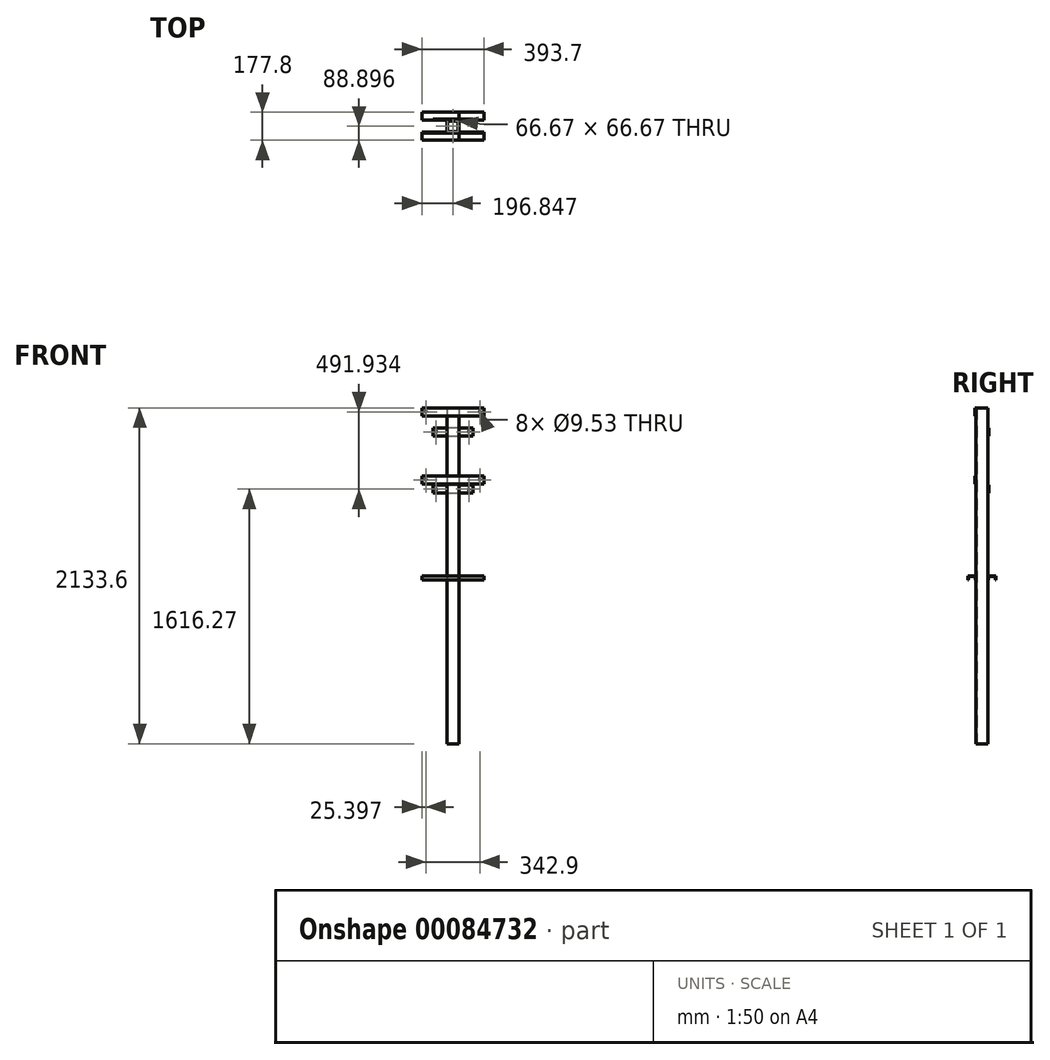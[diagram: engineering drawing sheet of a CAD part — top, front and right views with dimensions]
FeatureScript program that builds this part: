
annotation { "Feature Type Name" : "Feature", "Feature Type Description" : "" }
export const myFeature = defineFeature(function(context is Context, id is Id, definition is map)
    precondition{}
    {
        {
            var Q0;
            Q0=qCreatedBy(makeId("Top.planeOp"),FACE);
            var sketch = newSketch(context, id + "F0", { "sketchPlane" : qUnion([Q0])});
            skLineSegment(sketch, "E0.bottom", {"start": v(-38.12, 37.72) * mm, "end": v(38.08, 37.72) * mm});
            skLineSegment(sketch, "E0.top", {"start": v(-38.12, -38.48) * mm, "end": v(38.08, -38.48) * mm});
            skLineSegment(sketch, "E0.left", {"start": v(-38.12, 37.72) * mm, "end": v(-38.12, -38.48) * mm});
            skLineSegment(sketch, "E0.right", {"start": v(38.08, 37.72) * mm, "end": v(38.08, -38.48) * mm});
            skLineSegment(sketch, "E1.0", {"start": v(-33.36, 32.95) * mm, "end": v(-33.36, -33.72) * mm});
            skLineSegment(sketch, "E1.1", {"start": v(-33.36, 32.95) * mm, "end": v(33.31, 32.95) * mm});
            skLineSegment(sketch, "E1.2", {"start": v(33.31, 32.95) * mm, "end": v(33.31, -33.72) * mm});
            skLineSegment(sketch, "E1.3", {"start": v(-33.36, -33.72) * mm, "end": v(33.31, -33.72) * mm});
            skSolve(sketch);
        }
        {
            var Q0;
            Q0=makeQuery(id+"F0.imprint","IMPRINT",FACE,{"disambiguationData":[TD([[makeQuery(id+"F0.imprint","IMPRINT",EDGE,{"derivedFrom":sQuery(id+"F0.wireOp",EDGE,"E0.bottom")}),-1.0]])]});
            extrude(context, id + "F1", {"entities" : qUnion([Q0]), "depth" : 2133.6 * mm});
        }
        {
            var Q0;
            Q0=makeQuery(id+"F1.opExtrude","CAP_FACE",FACE,{"disambiguationData":[OSD([sQuery(id+"F0.wireOp",EDGE,"E0.bottom"),sQuery(id+"F0.wireOp",EDGE,"E0.top"),sQuery(id+"F0.wireOp",EDGE,"E0.left"),sQuery(id+"F0.wireOp",EDGE,"E0.right"),sQuery(id+"F0.wireOp",EDGE,"E1.0"),sQuery(id+"F0.wireOp",EDGE,"E1.1"),sQuery(id+"F0.wireOp",EDGE,"E1.2"),sQuery(id+"F0.wireOp",EDGE,"E1.3")])],"isStart":false});
            var sketch = newSketch(context, id + "F2", { "sketchPlane" : qUnion([Q0])});
            skSolve(sketch);
        }
        {
            var Q0;
            Q0=makeQuery(id+"F2.imprint","IMPRINT",FACE,{"disambiguationData":[TD([[makeQuery(id+"F2.imprint","IMPRINT",EDGE,{"derivedFrom":makeQuery(id+"F1.opExtrude","CAP_EDGE",EDGE,{"disambiguationData":[OSD([sQuery(id+"F0.wireOp",EDGE,"E1.0")])],"isStart":false})}),1.0]])]});
            var sketch = newSketch(context, id + "F3", { "sketchPlane" : qUnion([Q0])});
            skSolve(sketch);
        }
        {
            var Q0;
            Q0=qSketchRegion(id+"F3",true);
            var Q1;
            Q1=makeQuery(id+"F2.imprint","IMPRINT",FACE,{"disambiguationData":[TD([[makeQuery(id+"F2.imprint","IMPRINT",EDGE,{"derivedFrom":makeQuery(id+"F1.opExtrude","CAP_EDGE",EDGE,{"disambiguationData":[OSD([sQuery(id+"F0.wireOp",EDGE,"E1.0")])],"isStart":false})}),1.0]])]});
            extrude(context, id + "F4", {"entities" : qUnion([Q0, Q1]), "oppositeDirection" : true, "depth" : 4.76 * mm});
        }
        {
            var Q0;
            Q0=makeQuery(id+"F1.opExtrude","SWEPT_FACE",FACE,{"disambiguationData":[OSD([sQuery(id+"F0.wireOp",EDGE,"E0.top")])]});
            var sketch = newSketch(context, id + "F5", { "sketchPlane" : qUnion([Q0])});
            skLineSegment(sketch, "E2", {"start": v(-38.12, 2133.6) * mm, "end": v(-196.87, 2133.6) * mm});
            skLineSegment(sketch, "E3", {"start": v(-196.87, 2133.6) * mm, "end": v(-196.87, 2082.8) * mm});
            skLineSegment(sketch, "E4", {"start": v(-196.87, 2082.8) * mm, "end": v(196.83, 2082.8) * mm});
            skLineSegment(sketch, "E5", {"start": v(196.83, 2082.8) * mm, "end": v(196.83, 2133.6) * mm});
            skLineSegment(sketch, "E6", {"start": v(-38.12, 2133.6) * mm, "end": v(38.08, 2133.6) * mm});
            skLineSegment(sketch, "E7", {"start": v(38.08, 2133.6) * mm, "end": v(196.83, 2133.6) * mm});
            skCircle(sketch, "E8", {"center": v(-171.47, 2108.2) * mm, "radius": 4.76 * mm});
            skCircle(sketch, "E9", {"center": v(171.43, 2108.2) * mm, "radius": 4.76 * mm});
            skLineSegment(sketch, "E10", {"start": v(-196.87, 1701.8) * mm, "end": v(-38.12, 1701.8) * mm});
            skLineSegment(sketch, "E11", {"start": v(-38.12, 1701.8) * mm, "end": v(38.08, 1701.8) * mm});
            skLineSegment(sketch, "E12", {"start": v(38.08, 1701.8) * mm, "end": v(196.83, 1701.8) * mm});
            skLineSegment(sketch, "E13", {"start": v(196.83, 1701.8) * mm, "end": v(196.83, 1650.99) * mm});
            skLineSegment(sketch, "E14", {"start": v(196.83, 1650.99) * mm, "end": v(-196.87, 1650.99) * mm});
            skLineSegment(sketch, "E15", {"start": v(-196.87, 1650.99) * mm, "end": v(-196.87, 1701.8) * mm});
            skCircle(sketch, "E16", {"center": v(171.43, 1676.4) * mm, "radius": 4.76 * mm});
            skCircle(sketch, "E17", {"center": v(-171.47, 1676.4) * mm, "radius": 4.76 * mm});
            skSolve(sketch);
        }
        {
            var Q0;
            {var subQ1=sQuery(id+"F5.wireOp",EDGE,"E10");Q0=makeQuery(id+"F5.imprint","IMPRINT",FACE,{"disambiguationData":[TD([[makeQuery(id+"F5.imprint","IMPRINT",EDGE,{"derivedFrom":subQ1}),-1.0]])]});}
            var Q1;
            {var subQ4=sQuery(id+"F5.wireOp",EDGE,"E12");Q1=makeQuery(id+"F5.imprint","IMPRINT",FACE,{"disambiguationData":[TD([[makeQuery(id+"F5.imprint","IMPRINT",EDGE,{"derivedFrom":subQ4}),-1.0]])]});}
            var Q2;
            {var subQ0=sQuery(id+"F5.wireOp",EDGE,"E11");Q2=makeQuery(id+"F5.imprint","IMPRINT",FACE,{"disambiguationData":[TD([[makeQuery(id+"F5.imprint","IMPRINT",EDGE,{"derivedFrom":subQ0}),-1.0]])]});}
            var Q3;
            {var subQ4=sQuery(id+"F5.wireOp",EDGE,"E2");Q3=makeQuery(id+"F5.imprint","IMPRINT",FACE,{"disambiguationData":[TD([[makeQuery(id+"F5.imprint","IMPRINT",EDGE,{"derivedFrom":subQ4}),1.0]])]});}
            var Q4;
            {var subQ6=sQuery(id+"F5.wireOp",EDGE,"E6");Q4=makeQuery(id+"F5.imprint","IMPRINT",FACE,{"disambiguationData":[TD([[makeQuery(id+"F5.imprint","IMPRINT",EDGE,{"derivedFrom":subQ6}),-1.0]])]});}
            var Q5;
            {var subQ1=sQuery(id+"F5.wireOp",EDGE,"E5");Q5=makeQuery(id+"F5.imprint","IMPRINT",FACE,{"disambiguationData":[TD([[makeQuery(id+"F5.imprint","IMPRINT",EDGE,{"derivedFrom":subQ1}),1.0]])]});}
            extrude(context, id + "F6", {"entities" : qUnion([Q0, Q1, Q2, Q3, Q4, Q5]), "operationType" : NewBodyOperationType.ADD, "depth" : 6.35 * mm});
        }
        {
            var Q0;
            Q0=makeQuery(id+"F1.opExtrude","SWEPT_FACE",FACE,{"disambiguationData":[OSD([sQuery(id+"F0.wireOp",EDGE,"E0.bottom")])]});
            var sketch = newSketch(context, id + "F7", { "sketchPlane" : qUnion([Q0])});
            skLineSegment(sketch, "E18", {"start": v(-126.98, 2006.6) * mm, "end": v(127.02, 2006.6) * mm});
            skLineSegment(sketch, "E19", {"start": v(127.02, 2006.6) * mm, "end": v(127.02, 1955.8) * mm});
            skLineSegment(sketch, "E20", {"start": v(127.02, 1955.8) * mm, "end": v(-126.98, 1955.8) * mm});
            skLineSegment(sketch, "E21", {"start": v(-126.98, 1955.8) * mm, "end": v(-126.98, 2006.6) * mm});
            skLineSegment(sketch, "E22", {"start": v(127.02, 1641.67) * mm, "end": v(127.02, 1590.87) * mm});
            skLineSegment(sketch, "E23", {"start": v(127.02, 1590.87) * mm, "end": v(-126.98, 1590.87) * mm});
            skLineSegment(sketch, "E24", {"start": v(-126.98, 1590.87) * mm, "end": v(-126.98, 1641.67) * mm});
            skLineSegment(sketch, "E25", {"start": v(127.02, 1641.67) * mm, "end": v(-126.98, 1641.67) * mm});
            skCircle(sketch, "E26", {"center": v(-101.58, 1981.2) * mm, "radius": 4.76 * mm});
            skCircle(sketch, "E27", {"center": v(106.39, 1981.2) * mm, "radius": 4.76 * mm});
            skCircle(sketch, "E28", {"center": v(-100.93, 1616.27) * mm, "radius": 4.76 * mm});
            skCircle(sketch, "E29", {"center": v(107.03, 1616.27) * mm, "radius": 4.76 * mm});
            skSolve(sketch);
        }
        {
            var Q0;
            {var subQ0=sQuery(id+"F7.wireOp",EDGE,"E21");Q0=makeQuery(id+"F7.imprint","IMPRINT",FACE,{"disambiguationData":[TD([[makeQuery(id+"F7.imprint","IMPRINT",EDGE,{"derivedFrom":subQ0}),-1.0]])]});}
            var Q1;
            {var subQ0=sQuery(id+"F7.wireOp",EDGE,"E19");Q1=makeQuery(id+"F7.imprint","IMPRINT",FACE,{"disambiguationData":[TD([[makeQuery(id+"F7.imprint","IMPRINT",EDGE,{"derivedFrom":subQ0}),-1.0]])]});}
            var Q2;
            {var subQ1=sQuery(id+"F7.wireOp",EDGE,"E22");Q2=makeQuery(id+"F7.imprint","IMPRINT",FACE,{"disambiguationData":[TD([[makeQuery(id+"F7.imprint","IMPRINT",EDGE,{"derivedFrom":subQ1}),-1.0]])]});}
            var Q3;
            {var subQ0=sQuery(id+"F7.wireOp",EDGE,"E18");var subQ1=sQuery(id+"F0.wireOp",EDGE,"E0.bottom");var subQ2=makeQuery(id+"F1.opExtrude","SWEPT_EDGE",EDGE,{"disambiguationData":[OSD([subQ1,sQuery(id+"F0.wireOp",EDGE,"E0.right")])]});var subQ3=makeQuery(id+"F7.imprint","INTERSECT",VERTEX,{"derivedFrom":[subQ2,subQ0]});Q3=makeQuery(id+"F7.imprint","IMPRINT",FACE,{"disambiguationData":[TD([[makeQuery(id+"F7.imprint","IMPRINT",EDGE,{"disambiguationData":[TD([[subQ3,-1.0]])],"derivedFrom":subQ0}),-1.0]])]});}
            var Q4;
            {var subQ0=sQuery(id+"F7.wireOp",EDGE,"E23");var subQ1=sQuery(id+"F0.wireOp",EDGE,"E0.bottom");var subQ2=makeQuery(id+"F1.opExtrude","SWEPT_EDGE",EDGE,{"disambiguationData":[OSD([subQ1,sQuery(id+"F0.wireOp",EDGE,"E0.left")])]});var subQ3=makeQuery(id+"F7.imprint","INTERSECT",VERTEX,{"derivedFrom":[subQ2,subQ0]});Q4=makeQuery(id+"F7.imprint","IMPRINT",FACE,{"disambiguationData":[TD([[makeQuery(id+"F7.imprint","IMPRINT",EDGE,{"disambiguationData":[TD([[subQ3,-1.0]])],"derivedFrom":subQ0}),-1.0]])]});}
            var Q5;
            {var subQ0=sQuery(id+"F7.wireOp",EDGE,"E24");Q5=makeQuery(id+"F7.imprint","IMPRINT",FACE,{"disambiguationData":[TD([[makeQuery(id+"F7.imprint","IMPRINT",EDGE,{"derivedFrom":subQ0}),-1.0]])]});}
            extrude(context, id + "F8", {"entities" : qUnion([Q0, Q1, Q2, Q3, Q4, Q5]), "operationType" : NewBodyOperationType.ADD, "depth" : 6.35 * mm});
        }
        {
            var Q0;
            Q0=makeQuery(id+"F1.opExtrude","SWEPT_FACE",FACE,{"disambiguationData":[OSD([sQuery(id+"F0.wireOp",EDGE,"E0.right")])]});
            var sketch = newSketch(context, id + "F9", { "sketchPlane" : qUnion([Q0])});
            skLineSegment(sketch, "E30", {"start": v(-38.48, 1066.8) * mm, "end": v(-89.28, 1066.8) * mm});
            skLineSegment(sketch, "E31", {"start": v(-89.28, 1066.8) * mm, "end": v(-89.28, 1041.4) * mm});
            skLineSegment(sketch, "E32", {"start": v(-89.28, 1041.4) * mm, "end": v(-86.1, 1041.4) * mm});
            skLineSegment(sketch, "E33", {"start": v(-86.1, 1041.4) * mm, "end": v(-86.1, 1063.62) * mm});
            skLineSegment(sketch, "E34", {"start": v(-86.1, 1063.62) * mm, "end": v(-41.66, 1063.62) * mm});
            skLineSegment(sketch, "E35", {"start": v(-41.66, 1063.62) * mm, "end": v(-41.66, 1041.4) * mm});
            skLineSegment(sketch, "E36", {"start": v(-41.66, 1041.4) * mm, "end": v(-38.48, 1041.4) * mm});
            skLineSegment(sketch, "E37", {"start": v(37.72, 1066.8) * mm, "end": v(88.52, 1066.8) * mm});
            skLineSegment(sketch, "E38", {"start": v(88.52, 1066.8) * mm, "end": v(88.52, 1041.4) * mm});
            skLineSegment(sketch, "E39", {"start": v(88.52, 1041.4) * mm, "end": v(85.34, 1041.4) * mm});
            skLineSegment(sketch, "E40", {"start": v(85.34, 1041.4) * mm, "end": v(85.34, 1063.62) * mm});
            skLineSegment(sketch, "E41", {"start": v(85.34, 1063.62) * mm, "end": v(40.9, 1063.62) * mm});
            skLineSegment(sketch, "E42", {"start": v(40.9, 1063.62) * mm, "end": v(40.9, 1041.4) * mm});
            skLineSegment(sketch, "E43", {"start": v(40.9, 1041.4) * mm, "end": v(37.72, 1041.4) * mm});
            skSolve(sketch);
        }
        {
            var Q0;
            Q0 = qSketchRegion(id + "F9", true);
            var Q1;
            {var subQ0=sQuery(id+"F9.wireOp",EDGE,"E30");Q1=makeQuery(id+"F9.imprint","IMPRINT",FACE,{"disambiguationData":[TD([[makeQuery(id+"F9.imprint","IMPRINT",EDGE,{"derivedFrom":subQ0}),1.0]])]});}
            var Q2;
            {var subQ0=sQuery(id+"F9.wireOp",EDGE,"E37");Q2=makeQuery(id+"F9.imprint","IMPRINT",FACE,{"disambiguationData":[TD([[makeQuery(id+"F9.imprint","IMPRINT",EDGE,{"derivedFrom":subQ0}),-1.0]])]});}
            extrude(context, id + "F10", {"entities" : qUnion([Q0, Q1, Q2]), "depth" : 158.75 * mm});
        }
        {
            var Q0;
            Q0 = qSketchRegion(id + "F9", true);
            var Q1;
            Q1=makeQuery(id+"F10.opExtrude","CAP_FACE",FACE,{"disambiguationData":[OSD([sQuery(id+"F0.wireOp",EDGE,"E0.bottom"),sQuery(id+"F0.wireOp",EDGE,"E0.right"),sQuery(id+"F9.wireOp",EDGE,"E37"),sQuery(id+"F9.wireOp",EDGE,"E38"),sQuery(id+"F9.wireOp",EDGE,"E39"),sQuery(id+"F9.wireOp",EDGE,"E40"),sQuery(id+"F9.wireOp",EDGE,"E41"),sQuery(id+"F9.wireOp",EDGE,"E42"),sQuery(id+"F9.wireOp",EDGE,"E43")])],"isStart":true});
            var Q2;
            Q2=makeQuery(id+"F10.opExtrude","CAP_FACE",FACE,{"disambiguationData":[OSD([sQuery(id+"F0.wireOp",EDGE,"E0.top"),sQuery(id+"F0.wireOp",EDGE,"E0.right"),sQuery(id+"F9.wireOp",EDGE,"E30"),sQuery(id+"F9.wireOp",EDGE,"E31"),sQuery(id+"F9.wireOp",EDGE,"E32"),sQuery(id+"F9.wireOp",EDGE,"E33"),sQuery(id+"F9.wireOp",EDGE,"E34"),sQuery(id+"F9.wireOp",EDGE,"E35"),sQuery(id+"F9.wireOp",EDGE,"E36")])],"isStart":true});
            extrude(context, id + "F11", {"entities" : qUnion([Q0, Q1, Q2]), "depth" : 234.95 * mm});
        }
    });
